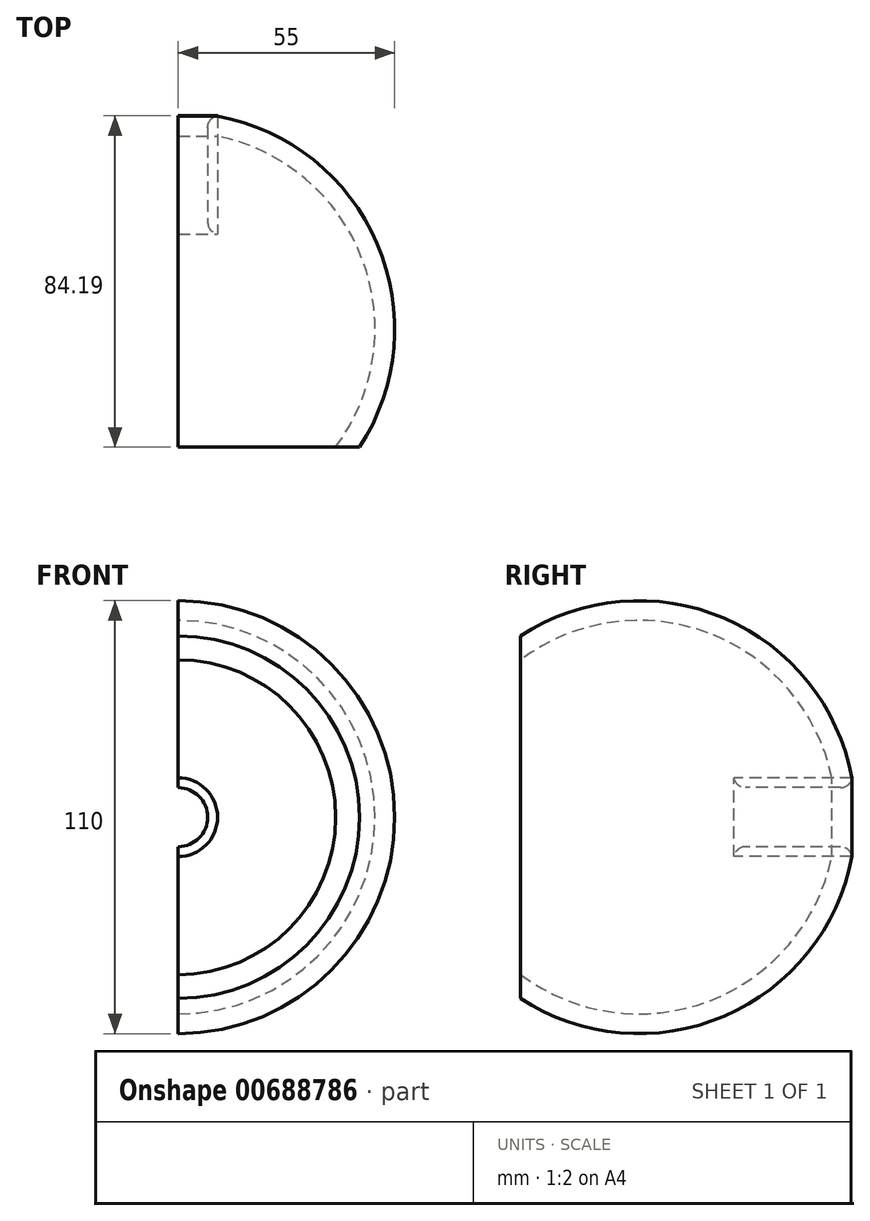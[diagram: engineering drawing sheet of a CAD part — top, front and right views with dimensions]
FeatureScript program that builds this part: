
annotation { "Feature Type Name" : "Feature", "Feature Type Description" : "" }
export const myFeature = defineFeature(function(context is Context, id is Id, definition is map)
    precondition{}
    {
        {
            var Q0;
            Q0=qCreatedBy(makeId("Top.planeOp"),FACE);
            var sketch = newSketch(context, id + "F0", { "sketchPlane" : qUnion([Q0])});
            skArc(sketch, "E0", {"start": v(0, 55) * mm, "mid": v(-55, 0) * mm, "end": v(0, -55) * mm});
            skLineSegment(sketch, "E1", {"start": v(0, 55) * mm, "end": v(0, 50) * mm});
            skArc(sketch, "E2", {"start": v(0, 50) * mm, "mid": v(-50, 0) * mm, "end": v(0, -50) * mm});
            skLineSegment(sketch, "E3.trimOffspring", {"start": v(0, -50) * mm, "end": v(0, -67.65) * mm});
            skPoint(sketch, "E4.orphan", {"position": v(0, 59.53) * mm});
            skSolve(sketch);
        }
        {
            var Q0;
            {var subQ0=sQuery(id+"F0.wireOp",EDGE,"E0");Q0=makeQuery(id+"F0.imprint","IMPRINT",FACE,{"disambiguationData":[TD([[makeQuery(id+"F0.imprint","IMPRINT",EDGE,{"derivedFrom":subQ0}),1.0]])]});}
            var Q1;
            Q1=sQuery(id+"F0.wireOp",EDGE,"E3.trimOffspring");
            revolve(context, id + "F1", {"entities" : qUnion([Q0]), "axis" : qUnion([Q1]), "revolveType" : RevolveType.FULL});
        }
        {
            var Q0;
            Q0=qCreatedBy(makeId("Front.planeOp"),FACE);
            var sketch = newSketch(context, id + "F2", { "sketchPlane" : qUnion([Q0])});
            skCircle(sketch, "E5", {"center": v(0, 0) * mm, "radius": 40 * mm});
            skSolve(sketch);
        }
        {
            var Q0;
            Q0=makeQuery(id+"F2.imprint","IMPRINT",FACE,{"disambiguationData":[TD([[makeQuery(id+"F2.imprint","IMPRINT",EDGE,{"derivedFrom":sQuery(id+"F2.wireOp",EDGE,"E5")}),1.0]])]});
            extrude(context, id + "F3", {"entities" : qUnion([Q0]), "depth" : 222.25 * mm, "offsetDistance" : 25 * mm});
        }
        {
            var Q0;
            Q0=makeQuery(id+"F3.opExtrude","SWEPT_BODY",BODY,{"disambiguationData":[OSD([sQuery(id+"F2.wireOp",EDGE,"E5")])]});
            transform(context, id + "F4", {"entities" : qUnion([Q0]), "transformType" : TransformType.TRANSLATION_3D, "dx" : 0 * mm, "dy" : -23.02 * mm, "dz" : 0 * mm, "makeCopy" : false});
        }
        {
            var Q0;
            Q0=qCreatedBy(makeId("Right.planeOp"),FACE);
            var sketch = newSketch(context, id + "F5", { "sketchPlane" : qUnion([Q0])});
            skLineSegment(sketch, "E6.bottom", {"start": v(-29.88, -56.3) * mm, "end": v(-104.59, -56.3) * mm});
            skLineSegment(sketch, "E6.top", {"start": v(-29.88, 62.38) * mm, "end": v(-104.59, 62.38) * mm});
            skLineSegment(sketch, "E6.left", {"start": v(-29.88, -56.3) * mm, "end": v(-29.88, 62.38) * mm});
            skLineSegment(sketch, "E6.right", {"start": v(-104.59, -56.3) * mm, "end": v(-104.59, 62.38) * mm});
            skSolve(sketch);
        }
        {
            var Q0;
            Q0=makeQuery(id+"F5.imprint","IMPRINT",FACE,{"disambiguationData":[TD([[makeQuery(id+"F5.imprint","IMPRINT",EDGE,{"derivedFrom":sQuery(id+"F5.wireOp",EDGE,"E6.bottom")}),-1.0]])]});
            extrude(context, id + "F6", {"entities" : qUnion([Q0]), "depth" : 146.77 * mm, "offsetDistance" : 25 * mm, "hasSecondDirection" : true, "secondDirectionOppositeDirection" : true, "secondDirectionDepth" : 173.4 * mm});
        }
        {
            var Q0;
            Q0=makeQuery(id+"F3.opExtrude","SWEPT_BODY",BODY,{"disambiguationData":[OSD([sQuery(id+"F2.wireOp",EDGE,"E5")])]});
            var Q1;
            Q1=makeQuery(id+"F1.opRevolve","SWEPT_BODY",BODY,{"disambiguationData":[OSD([sQuery(id+"F0.wireOp",EDGE,"E0"),sQuery(id+"F0.wireOp",EDGE,"E1"),sQuery(id+"F0.wireOp",EDGE,"E2"),sQuery(id+"F0.wireOp",EDGE,"E3.trimOffspring")])]});
            booleanBodies(context, id + "F7", {"operationType" : BooleanOperationType.SUBTRACTION, "tools" : qUnion([Q0]), "targets" : qUnion([Q1])});
        }
        {
            var Q0;
            Q0=makeQuery(id+"F6.opExtrude","SWEPT_BODY",BODY,{"disambiguationData":[OSD([sQuery(id+"F5.wireOp",EDGE,"E6.bottom"),sQuery(id+"F5.wireOp",EDGE,"E6.top"),sQuery(id+"F5.wireOp",EDGE,"E6.left"),sQuery(id+"F5.wireOp",EDGE,"E6.right")])]});
            transform(context, id + "F8", {"entities" : qUnion([Q0]), "transformType" : TransformType.TRANSLATION_3D, "dx" : 0 * mm, "dy" : -0.17 * mm, "dz" : 0 * mm, "makeCopy" : false});
        }
        {
            var Q0;
            Q0=makeQuery(id+"F6.opExtrude","SWEPT_BODY",BODY,{"disambiguationData":[OSD([sQuery(id+"F5.wireOp",EDGE,"E6.bottom"),sQuery(id+"F5.wireOp",EDGE,"E6.top"),sQuery(id+"F5.wireOp",EDGE,"E6.left"),sQuery(id+"F5.wireOp",EDGE,"E6.right")])]});
            var Q1;
            Q1=makeQuery(id+"F1.opRevolve","SWEPT_BODY",BODY,{"disambiguationData":[OSD([sQuery(id+"F0.wireOp",EDGE,"E0"),sQuery(id+"F0.wireOp",EDGE,"E1"),sQuery(id+"F0.wireOp",EDGE,"E2"),sQuery(id+"F0.wireOp",EDGE,"E3.trimOffspring")])]});
            booleanBodies(context, id + "F9", {"operationType" : BooleanOperationType.SUBTRACTION, "tools" : qUnion([Q0]), "targets" : qUnion([Q1])});
        }
        {
            var Q0;
            Q0=qCreatedBy(makeId("Front.planeOp"),FACE);
            var sketch = newSketch(context, id + "F10", { "sketchPlane" : qUnion([Q0])});
            skCircle(sketch, "E7", {"center": v(0, 0) * mm, "radius": 12.5 * mm});
            skSolve(sketch);
        }
        {
            var Q0;
            Q0=sQuery(id+"F10.wireOp",VERTEX,"E7.center");
            var Q1;
            Q1=makeQuery(id+"F1.opRevolve","SWEPT_BODY",BODY,{"disambiguationData":[OSD([sQuery(id+"F0.wireOp",EDGE,"E0"),sQuery(id+"F0.wireOp",EDGE,"E1"),sQuery(id+"F0.wireOp",EDGE,"E2"),sQuery(id+"F0.wireOp",EDGE,"E3.trimOffspring")])]});
            hole(context, id + "F11", {"style" : HoleStyle.SIMPLE, "endStyle" : HoleEndStyle.THROUGH, "holeDiameter" : 20 * mm, "majorDiameter" : 5 * mm, "isTappedThrough" : true, "tappedDepth" : 12 * mm, "tapClearance" : 3, "locations" : qUnion([Q0]), "scope" : qUnion([Q1])});
        }
        {
            var Q0;
            Q0=qCreatedBy(makeId("Front.planeOp"),FACE);
            var sketch = newSketch(context, id + "F12", { "sketchPlane" : qUnion([Q0])});
            skCircle(sketch, "E8", {"center": v(0, 0) * mm, "radius": 10 * mm});
            skCircle(sketch, "E9", {"center": v(0, 0) * mm, "radius": 7.5 * mm});
            skSolve(sketch);
        }
        {
            var Q0;
            Q0=makeQuery(id+"F12.imprint","IMPRINT",FACE,{"disambiguationData":[TD([[makeQuery(id+"F12.imprint","IMPRINT",EDGE,{"derivedFrom":sQuery(id+"F12.wireOp",EDGE,"E8")}),1.0]])]});
            extrude(context, id + "F13", {"entities" : qUnion([Q0]), "oppositeDirection" : true, "depth" : 30 * mm, "offsetDistance" : 25 * mm});
        }
        {
            var Q0;
            Q0=makeQuery(id+"F13.opExtrude","SWEPT_BODY",BODY,{"disambiguationData":[OSD([sQuery(id+"F12.wireOp",EDGE,"E8"),sQuery(id+"F12.wireOp",EDGE,"E9")])]});
            transform(context, id + "F14", {"entities" : qUnion([Q0]), "transformType" : TransformType.TRANSLATION_3D, "dx" : 0 * mm, "dy" : 24.14 * mm, "dz" : 0 * mm, "makeCopy" : false});
        }
        {
            var Q0;
            Q0=makeQuery(id+"F13.opExtrude","CAP_EDGE",EDGE,{"disambiguationData":[OSD([sQuery(id+"F12.wireOp",EDGE,"E9")])],"isStart":false});
            fillet(context, id + "F15", {"entities" : qUnion([Q0]), "radius" : 3 * mm, "tangentPropagation" : true, "allowEdgeOverflow" : false});
        }
        {
            var Q0;
            Q0=makeQuery(id+"F13.opExtrude","CAP_EDGE",EDGE,{"disambiguationData":[OSD([sQuery(id+"F12.wireOp",EDGE,"E9")])],"isStart":true});
            fillet(context, id + "F16", {"entities" : qUnion([Q0]), "radius" : 3 * mm, "tangentPropagation" : true, "allowEdgeOverflow" : false});
        }
        {
            var Q0;
            Q0=qCreatedBy(makeId("Right.planeOp"),FACE);
            var sketch = newSketch(context, id + "F17", { "sketchPlane" : qUnion([Q0])});
            skLineSegment(sketch, "E10.bottom", {"start": v(-61.26, 62.44) * mm, "end": v(65.84, 62.44) * mm});
            skLineSegment(sketch, "E10.top", {"start": v(-61.26, -64.21) * mm, "end": v(65.84, -64.21) * mm});
            skLineSegment(sketch, "E10.left", {"start": v(-61.26, 62.44) * mm, "end": v(-61.26, -64.21) * mm});
            skLineSegment(sketch, "E10.right", {"start": v(65.84, 62.44) * mm, "end": v(65.84, -64.21) * mm});
            skSolve(sketch);
        }
        {
            var Q0;
            Q0 = qSketchRegion(id + "F17", true);
            extrude(context, id + "F18", {"entities" : qUnion([Q0]), "operationType" : NewBodyOperationType.REMOVE, "oppositeDirection" : true, "depth" : 82.69 * mm, "offsetDistance" : 25 * mm});
        }
    });
